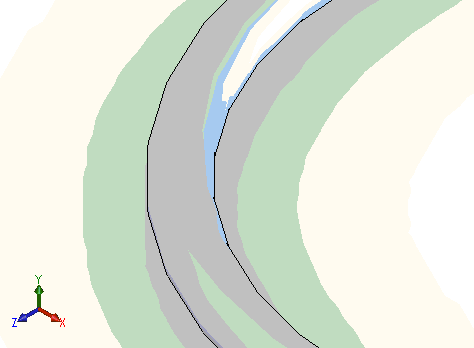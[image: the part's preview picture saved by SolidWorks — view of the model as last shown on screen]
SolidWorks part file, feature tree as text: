
SOLIDWORKS PART (.sldprt)
format: sldprt  version: not decoded by parser v0  size: 296,448 bytes
history: native  units: mm
features: sketch x10, cut_extrude x6, extrude x2, material x1, sweep x1 + 1 further entry (+14 scaffold rows collapsed)
feature tree (35):
  scaffold x14  (default folders/planes/origin — collapsed)
  material  "Material <not specified>"
  "Annotations"  RD1=18.72mm RD4=15.98mm
  sketch  "Sketch1"  dims[D1=7.875mm]
  extrude  "Extrude1"  Depth=812.2mm
  sketch  "Sketch2"  dims[D1=9.252mm]
  cut_extrude  "Cut-Extrude1"  [1 undecoded]
  sketch  "Sketch3"  dims[D1=3.175mm]
  cut_extrude  "Cut-Extrude2"  [1 undecoded]
  sketch  "Sketch6"
  sketch  "Sketch7"  dims[D1=9.36mm]
  sketch  "Sketch10"  dims[D1=9.525mm]
  cut_extrude  "Cut-Extrude3"  [1 undecoded]
  sketch  "Sketch11"  dims[D1=~7.989998mm]
  cut_extrude  "Cut-Extrude4"  [1 undecoded]
  sweep  "Sweep3"
  sketch  "Sketch12"
  extrude  "Extrude2"  Depth=25mm
  sketch  "Sketch13"
  cut_extrude  "Cut-Extrude5"  [1 undecoded]
  sketch  "Sketch15"  dims[D1=3.175mm]
  cut_extrude  "Cut-Extrude6"  [1 undecoded]
decode coverage: 9 of 19 modeling features carry decoded parameters; 1 rows unclassified (native names shown)
note: ~ marks probable driven/reference dimensions
note: 6 parameter values undecoded
summary: no parameter record found for 6 features
note: suppression state not decoded; provenance and decode notes live in map.json
